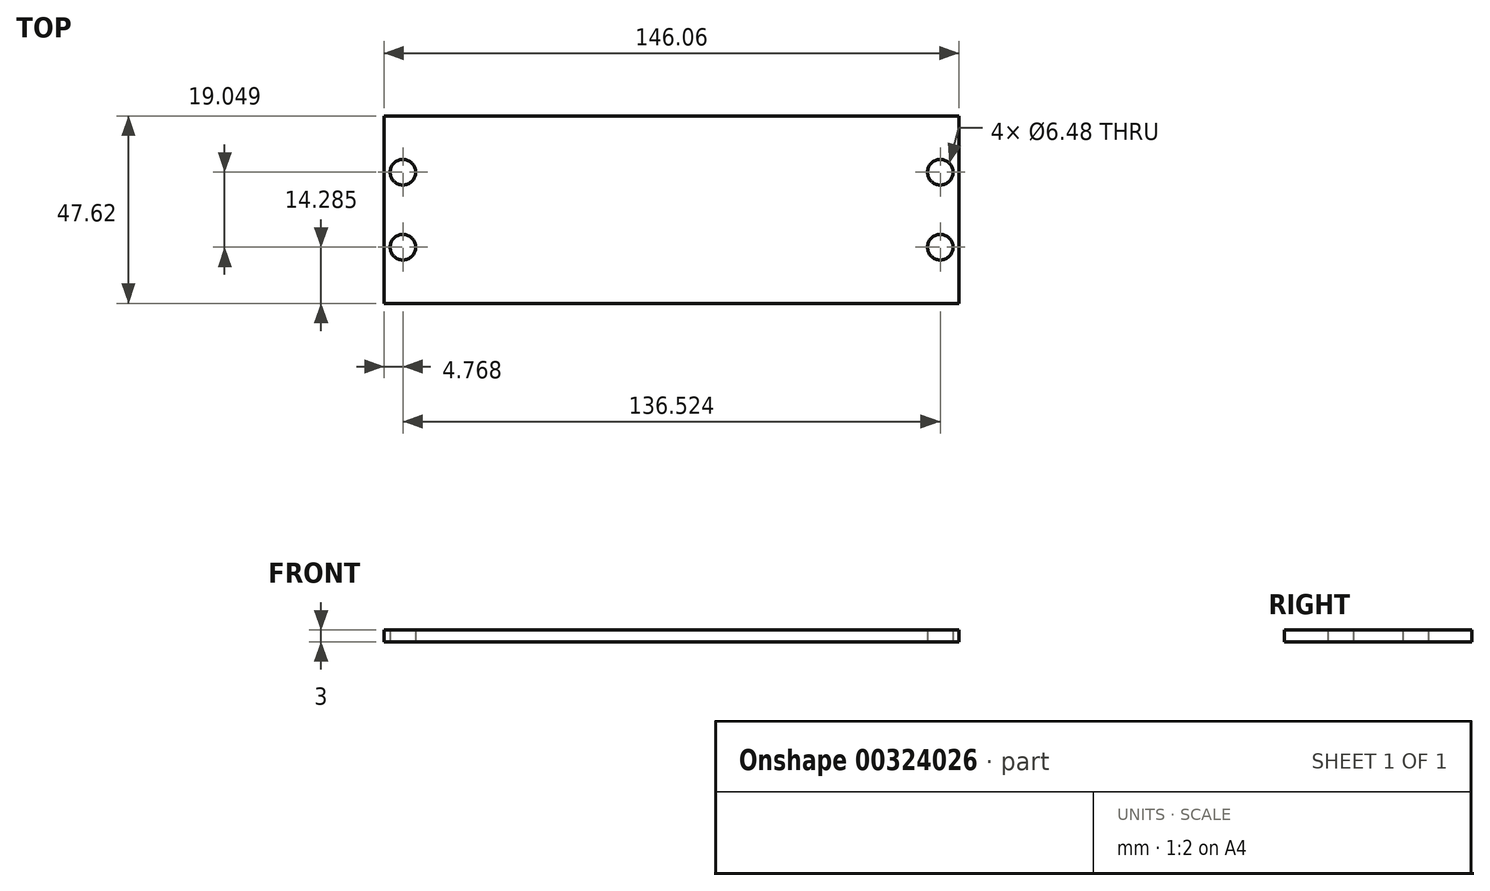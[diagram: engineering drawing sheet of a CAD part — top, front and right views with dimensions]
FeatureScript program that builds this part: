
annotation { "Feature Type Name" : "Feature", "Feature Type Description" : "" }
export const myFeature = defineFeature(function(context is Context, id is Id, definition is map)
    precondition{}
    {
        {
            var Q0;
            Q0=qCreatedBy(makeId("Top.planeOp"),FACE);
            var sketch = newSketch(context, id + "F0", { "sketchPlane" : qUnion([Q0])});
            skLineSegment(sketch, "E0", {"start": v(72.22, -23.01) * mm, "end": v(72.22, -15.86) * mm});
            skLineSegment(sketch, "E1", {"start": v(72.22, -3.19) * mm, "end": v(72.22, 3.17) * mm});
            skLineSegment(sketch, "E2", {"start": v(-68.2, -15.87) * mm, "end": v(-72.23, -15.87) * mm});
            skLineSegment(sketch, "E3", {"start": v(-68.26, 15.87) * mm, "end": v(-72.23, 15.87) * mm});
            skLineSegment(sketch, "E4", {"start": v(68.26, 15.87) * mm, "end": v(72.22, 15.87) * mm});
            skLineSegment(sketch, "E5", {"start": v(-68.26, 3.17) * mm, "end": v(-72.23, 3.17) * mm});
            skLineSegment(sketch, "E6", {"start": v(68.26, 3.17) * mm, "end": v(72.22, 3.17) * mm});
            skLineSegment(sketch, "E7", {"start": v(67.83, -3.19) * mm, "end": v(72.22, -3.19) * mm});
            skArc(sketch, "E8", {"start": v(67.83, -3.19) * mm, "mid": v(61.93, -9.96) * mm, "end": v(68.7, -15.86) * mm});
            skLineSegment(sketch, "E9", {"start": v(68.7, -15.86) * mm, "end": v(72.22, -15.86) * mm});
            skLineSegment(sketch, "E10", {"start": v(-68.33, -3.17) * mm, "end": v(-72.23, -3.17) * mm});
            skArc(sketch, "E11", {"start": v(68.26, 15.87) * mm, "mid": v(61.91, 9.52) * mm, "end": v(68.26, 3.17) * mm});
            skLineSegment(sketch, "E12", {"start": v(72.22, 15.87) * mm, "end": v(72.22, 23.01) * mm});
            skLineSegment(sketch, "E13", {"start": v(-72.23, -3.17) * mm, "end": v(-72.23, 3.17) * mm});
            skLineSegment(sketch, "E14", {"start": v(-72.23, 15.87) * mm, "end": v(-72.23, 23.01) * mm});
            skLineSegment(sketch, "E15", {"start": v(72.22, -23.01) * mm, "end": v(-72.23, -23.01) * mm});
            skArc(sketch, "E16", {"start": v(-68.26, 3.17) * mm, "mid": v(-61.91, 9.52) * mm, "end": v(-68.26, 15.87) * mm});
            skLineSegment(sketch, "E17", {"start": v(-72.23, 23.01) * mm, "end": v(72.23, 23.01) * mm});
            skArc(sketch, "E18", {"start": v(-68.2, -15.87) * mm, "mid": v(-61.91, -9.46) * mm, "end": v(-68.33, -3.17) * mm});
            skLineSegment(sketch, "E19", {"start": v(-72.23, -23.01) * mm, "end": v(-72.23, -15.87) * mm});
            skCircle(sketch, "E20", {"center": v(68.26, -9.52) * mm, "radius": 3.24 * mm});
            skCircle(sketch, "E21", {"center": v(-68.26, 9.52) * mm, "radius": 3.24 * mm});
            skLineSegment(sketch, "E22", {"start": v(-73.03, -23.81) * mm, "end": v(-73.03, 23.81) * mm});
            skCircle(sketch, "E23", {"center": v(-68.26, -9.52) * mm, "radius": 3.24 * mm});
            skLineSegment(sketch, "E24", {"start": v(73.03, -23.81) * mm, "end": v(73.03, 23.81) * mm});
            skLineSegment(sketch, "E25", {"start": v(-73.03, 23.81) * mm, "end": v(73.03, 23.81) * mm});
            skLineSegment(sketch, "E26", {"start": v(73.03, -23.81) * mm, "end": v(-73.03, -23.81) * mm});
            skCircle(sketch, "E27", {"center": v(68.26, 9.52) * mm, "radius": 3.24 * mm});
            skSolve(sketch);
        }
        {
            var Q0;
            Q0 = qSketchRegion(id + "F0", true);
            var Q1;
            Q1=makeQuery(id+"F0.imprint","IMPRINT",FACE,{"disambiguationData":[TD([[makeQuery(id+"F0.imprint","IMPRINT",EDGE,{"derivedFrom":sQuery(id+"F0.wireOp",EDGE,"E0")}),1.0]])]});
            extrude(context, id + "F1", {"entities" : qUnion([Q0, Q1]), "depth" : 3 * mm});
        }
    });
